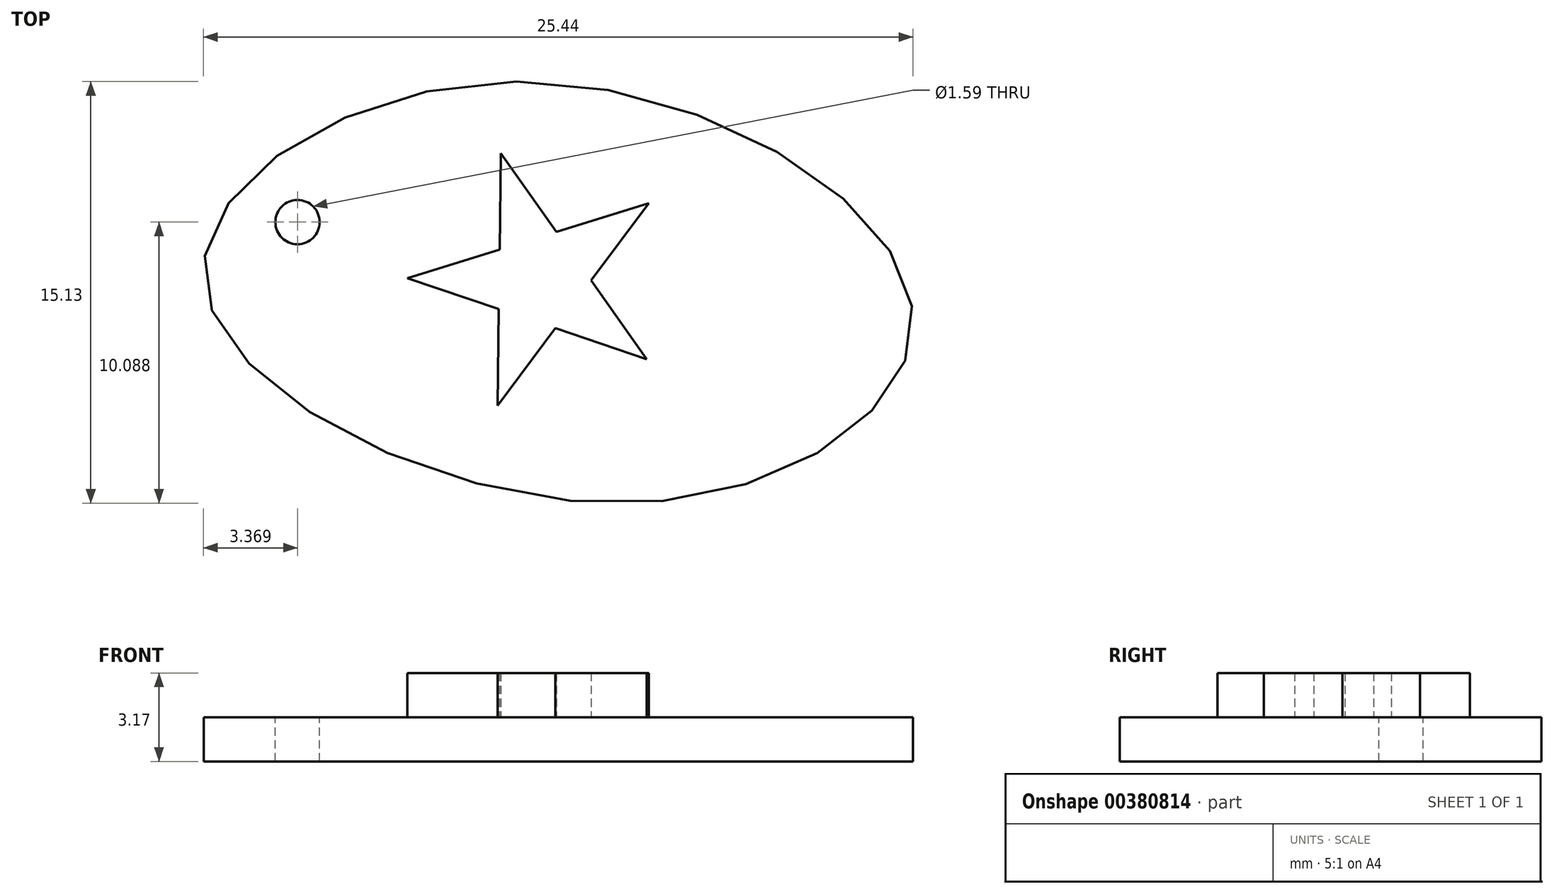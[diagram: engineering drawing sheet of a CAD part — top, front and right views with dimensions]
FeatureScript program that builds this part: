
annotation { "Feature Type Name" : "Feature", "Feature Type Description" : "" }
export const myFeature = defineFeature(function(context is Context, id is Id, definition is map)
    precondition{}
    {
        {
            var Q0;
            Q0=qCreatedBy(makeId("Top.planeOp"),FACE);
            var sketch = newSketch(context, id + "F0", { "sketchPlane" : qUnion([Q0])});
            skFitSpline(sketch, "E0", {"points": [v(0, 0) * mm, v(14.2, -8.2) * mm, v(4.35, -15.12) * mm, v(-11.2, -7.16) * mm, v(0, 0) * mm]});
            skSolve(sketch);
        }
        {
            var Q0;
            Q0 = qSketchRegion(id + "F0", true);
            extrude(context, id + "F1", {"entities" : qUnion([Q0]), "depth" : 1.59 * mm});
        }
        {
            var Q0;
            Q0=makeQuery(id+"F1.opExtrude","CAP_FACE",FACE,{"disambiguationData":[OSD([sQuery(id+"F0.wireOp",EDGE,"E0")])],"isStart":false});
            var sketch = newSketch(context, id + "F2", { "sketchPlane" : qUnion([Q0])});
            skCircle(sketch, "E1.cCircle", {"center": v(0.86, -7.11) * mm, "radius": 4.76 * mm, "construction": true});
            skLineSegment(sketch, "E1.0", {"start": v(4.67, -9.96) * mm, "end": v(-0.67, -11.63) * mm});
            skLineSegment(sketch, "E1.1", {"start": v(-0.67, -11.63) * mm, "end": v(-3.9, -7.05) * mm});
            skLineSegment(sketch, "E1.2", {"start": v(-3.9, -7.05) * mm, "end": v(-0.56, -2.57) * mm});
            skLineSegment(sketch, "E1.3", {"start": v(-0.56, -2.57) * mm, "end": v(4.74, -4.36) * mm});
            skLineSegment(sketch, "E1.4", {"start": v(4.74, -4.36) * mm, "end": v(4.67, -9.96) * mm});
            skLineSegment(sketch, "E2", {"start": v(-0.67, -11.63) * mm, "end": v(-0.56, -2.57) * mm});
            skLineSegment(sketch, "E3", {"start": v(4.67, -9.96) * mm, "end": v(-0.56, -2.57) * mm});
            skLineSegment(sketch, "E4", {"start": v(4.67, -9.96) * mm, "end": v(-3.9, -7.05) * mm});
            skLineSegment(sketch, "E5", {"start": v(-3.9, -7.05) * mm, "end": v(4.74, -4.36) * mm});
            skLineSegment(sketch, "E6", {"start": v(4.74, -4.36) * mm, "end": v(-0.67, -11.63) * mm});
            skSolve(sketch);
        }
        {
            var Q0;
            {var subQ1=sQuery(id+"F2.wireOp",EDGE,"E2");var subQ5=sQuery(id+"F2.wireOp",EDGE,"E4");var subQ6=makeQuery(id+"F2.imprint","INTERSECT",VERTEX,{"derivedFrom":[subQ1,subQ5]});Q0=makeQuery(id+"F2.imprint","IMPRINT",FACE,{"disambiguationData":[TD([[makeQuery(id+"F2.imprint","IMPRINT",EDGE,{"disambiguationData":[TD([[subQ6,-1.0]])],"derivedFrom":subQ1}),-1.0]])]});}
            var Q1;
            {var subQ1=sQuery(id+"F2.wireOp",EDGE,"E3");var subQ3=sQuery(id+"F2.wireOp",EDGE,"E6");var subQ4=makeQuery(id+"F2.imprint","INTERSECT",VERTEX,{"derivedFrom":[subQ1,subQ3]});Q1=makeQuery(id+"F2.imprint","IMPRINT",FACE,{"disambiguationData":[TD([[makeQuery(id+"F2.imprint","IMPRINT",EDGE,{"disambiguationData":[TD([[subQ4,-1.0]])],"derivedFrom":subQ3}),1.0]])]});}
            var Q2;
            {var subQ1=sQuery(id+"F2.wireOp",EDGE,"E2");var subQ3=sQuery(id+"F2.wireOp",EDGE,"E4");var subQ4=makeQuery(id+"F2.imprint","INTERSECT",VERTEX,{"derivedFrom":[subQ1,subQ3]});Q2=makeQuery(id+"F2.imprint","IMPRINT",FACE,{"disambiguationData":[TD([[makeQuery(id+"F2.imprint","IMPRINT",EDGE,{"disambiguationData":[TD([[subQ4,1.0]])],"derivedFrom":subQ3}),1.0]])]});}
            var Q3;
            {var subQ0=sQuery(id+"F2.wireOp",EDGE,"E4");var subQ1=sQuery(id+"F2.wireOp",EDGE,"E2");var subQ2=makeQuery(id+"F2.imprint","INTERSECT",VERTEX,{"derivedFrom":[subQ1,subQ0]});Q3=makeQuery(id+"F2.imprint","IMPRINT",FACE,{"disambiguationData":[TD([[makeQuery(id+"F2.imprint","IMPRINT",EDGE,{"disambiguationData":[TD([[subQ2,-1.0]])],"derivedFrom":subQ1}),1.0]])]});}
            var Q4;
            {var subQ0=sQuery(id+"F2.wireOp",EDGE,"E6");var subQ1=sQuery(id+"F2.wireOp",EDGE,"E3");var subQ2=makeQuery(id+"F2.imprint","INTERSECT",VERTEX,{"derivedFrom":[subQ1,subQ0]});Q4=makeQuery(id+"F2.imprint","IMPRINT",FACE,{"disambiguationData":[TD([[makeQuery(id+"F2.imprint","IMPRINT",EDGE,{"disambiguationData":[TD([[subQ2,-1.0]])],"derivedFrom":subQ1}),-1.0]])]});}
            var Q5;
            {var subQ1=sQuery(id+"F2.wireOp",EDGE,"E2");var subQ3=sQuery(id+"F2.wireOp",EDGE,"E5");var subQ4=makeQuery(id+"F2.imprint","INTERSECT",VERTEX,{"derivedFrom":[subQ1,subQ3]});Q5=makeQuery(id+"F2.imprint","IMPRINT",FACE,{"disambiguationData":[TD([[makeQuery(id+"F2.imprint","IMPRINT",EDGE,{"disambiguationData":[TD([[subQ4,-1.0]])],"derivedFrom":subQ3}),1.0]])]});}
            var Q6;
            Q6=sQuery(id+"F2.wireOp",EDGE,"E4");
            var Q7;
            Q7=sQuery(id+"F2.wireOp",EDGE,"E5");
            var Q8;
            Q8=sQuery(id+"F2.wireOp",EDGE,"E2");
            var Q9;
            Q9=sQuery(id+"F2.wireOp",EDGE,"E3");
            var Q10;
            Q10=sQuery(id+"F2.wireOp",EDGE,"E6");
            extrude(context, id + "F3", {"entities" : qUnion([Q0, Q1, Q2, Q3, Q4, Q5]), "operationType" : NewBodyOperationType.ADD, "surfaceEntities" : qUnion([Q6, Q7, Q8, Q9, Q10]), "depth" : 1.59 * mm});
        }
        {
            var Q0;
            Q0=makeQuery(id+"F1.opExtrude","CAP_FACE",FACE,{"disambiguationData":[OSD([sQuery(id+"F0.wireOp",EDGE,"E0")])],"isStart":false});
            var sketch = newSketch(context, id + "F4", { "sketchPlane" : qUnion([Q0])});
            skCircle(sketch, "E7", {"center": v(-7.85, -5.04) * mm, "radius": 0.8 * mm});
            skSolve(sketch);
        }
        {
            var Q0;
            Q0 = qSketchRegion(id + "F4", true);
            extrude(context, id + "F5", {"entities" : qUnion([Q0]), "operationType" : NewBodyOperationType.REMOVE, "oppositeDirection" : true, "depth" : 25.4 * mm});
        }
    });
